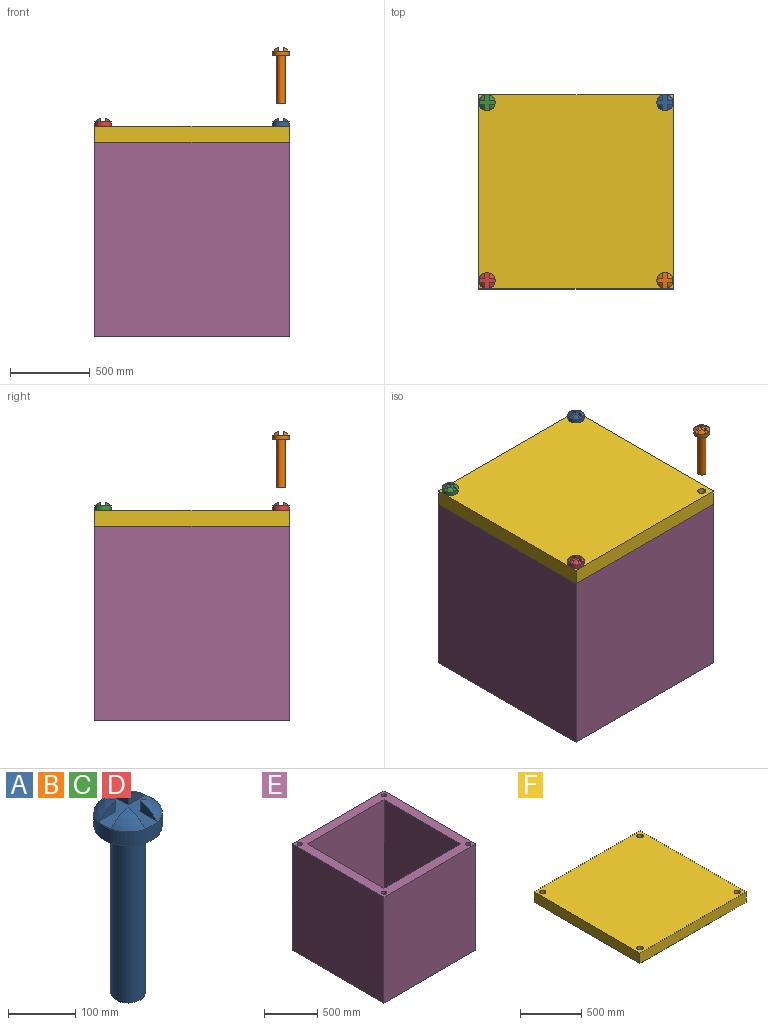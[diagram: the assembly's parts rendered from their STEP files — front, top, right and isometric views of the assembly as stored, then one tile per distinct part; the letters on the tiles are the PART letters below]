
ASSEMBLY  parts=6 mates=5
PART A: 14 faces, bbox 101.6x101.6x352.2 mm
  f0: revolved ~101.6x101.6mm, area 4783.2mm2, adj f4,f5,f6,f7,f8,f9,f10,f11
  f1: plane 50.8x50.8mm, normal (0,0,-1), area 2026.8mm2, adj f2
  f2: cylinder r=25.4mm len=304.8mm, axis (0,0,1), area 48643.9mm2, adj f1,f3
  f3: plane 101.6x101.6mm, normal (0,0,-1), area 6080.5mm2, adj f2,f4
  f4: cylinder r=50.8mm len=101.6mm, axis (0,0,1), area 8107.3mm2, adj f0,f3
  f5: plane 35.99x21.41mm, normal (0,1,0), area 474.5mm2, adj f0,f6,f13
  f6: plane 35.99x21.41mm, normal (1,0,0), area 474.5mm2, adj f0,f5,f13
  f7: plane 35.99x21.41mm, normal (-1,0,0), area 474.5mm2, adj f0,f8,f13
  f8: plane 35.99x21.41mm, normal (0,1,0), area 474.5mm2, adj f0,f7,f13
  f9: plane 35.99x21.41mm, normal (0,-1,0), area 474.5mm2, adj f0,f10,f13
  f10: plane 35.99x21.41mm, normal (-1,0,0), area 474.5mm2, adj f0,f9,f13
  f11: plane 35.99x21.41mm, normal (1,0,0), area 474.5mm2, adj f0,f12,f13
  f12: plane 35.99x21.41mm, normal (0,-1,0), area 474.5mm2, adj f0,f11,f13
  f13: plane 100.6x100.6mm, normal (0,0,1), area 4410.5mm2, adj f0,f5,f6,f7,f8,f9,f10,f11
PART B: same geometry as A
PART C: same geometry as A
PART D: same geometry as A
PART E: 19 faces, bbox 1219.2x1219.2x1219.2 mm
  f0: plane 1219.2x1219.2mm, normal (0,0,1), area 446085.3mm2, adj f1,f2,f3,f4,f6,f7,f8,f9
  f1: plane 1219.2x1219.2mm, normal (1,0,0), area 1486448.6mm2, adj f0,f2,f4,f5
  f2: plane 1219.2x1219.2mm, normal (0,1,0), area 1486448.6mm2, adj f0,f1,f3,f5
  f3: plane 1219.2x1219.2mm, normal (-1,0,0), area 1486448.6mm2, adj f0,f2,f4,f5
  f4: plane 1219.2x1219.2mm, normal (0,-1,0), area 1486448.6mm2, adj f0,f1,f3,f5
  f5: plane 1219.2x1219.2mm, normal (0,0,-1), area 1486448.6mm2, adj f1,f2,f3,f4
  f6: plane 1117.6x1016mm, normal (-1,0,0), area 1135481.6mm2, adj f0,f7,f9,f10
  f7: plane 1117.6x1016mm, normal (0,-1,0), area 1135481.6mm2, adj f0,f6,f8,f10
  f8: plane 1117.6x1016mm, normal (1,0,0), area 1135481.6mm2, adj f0,f7,f9,f10
  f9: plane 1117.6x1016mm, normal (0,1,0), area 1135481.6mm2, adj f0,f6,f8,f10
  f10: plane 1016x1016mm, normal (0,0,1), area 1032256mm2, adj f6,f7,f8,f9
  f11: cylinder r=25.4mm len=254mm, axis (0,0,1), area 40536.6mm2, adj f0,f12
  f12: plane 50.8x50.8mm, normal (0,0,1), area 2026.8mm2, adj f11
  f13: cylinder r=25.4mm len=254mm, axis (0,0,1), area 40536.6mm2, adj f0,f14
  f14: plane 50.8x50.8mm, normal (0,0,1), area 2026.8mm2, adj f13
  f15: cylinder r=25.4mm len=254mm, axis (0,0,1), area 40536.6mm2, adj f0,f16
  f16: plane 50.8x50.8mm, normal (0,0,1), area 2026.8mm2, adj f15
  f17: cylinder r=25.4mm len=254mm, axis (0,0,1), area 40536.6mm2, adj f0,f18
  f18: plane 50.8x50.8mm, normal (0,0,1), area 2026.8mm2, adj f17
PART F: 25 faces, bbox 1219.2x1219.2x203.2 mm
  f0: plane 1219.2x1219.2mm, normal (0,0,1), area 1478341.3mm2, adj f9,f10,f11,f12,f21,f22,f23,f24
  f1: plane 1219.2x1219.2mm, normal (0,0,-1), area 446085.3mm2, adj f4,f6,f9,f10,f11,f12,f13,f14
  f2: plane 1016x25.4mm, normal (-1,0,0), area 25806.4mm2, adj f8,f15,f16,f17
  f3: plane 965.2x50.8mm, normal (0,1,0), area 49032.2mm2, adj f17,f18,f19,f20
  f4: plane 1016x25.4mm, normal (1,0,0), area 25806.4mm2, adj f1,f6,f13,f18
  f5: plane 965.2x50.8mm, normal (0,-1,0), area 49032.2mm2, adj f17,f18,f19,f20
  f6: plane 1016x25.4mm, normal (0,1,0), area 25806.4mm2, adj f1,f4,f14,f18
  f7: plane 1016x25.4mm, normal (1,0,0), area 25806.4mm2, adj f8,f15,f16,f17
  f8: plane 1016x25.4mm, normal (0,-1,0), area 25806.4mm2, adj f2,f7,f16,f17
  f9: plane 1219.2x101.6mm, normal (1,0,0), area 123870.7mm2, adj f0,f1,f10,f12
  f10: plane 1219.2x101.6mm, normal (0,1,0), area 123870.7mm2, adj f0,f1,f9,f11
  f11: plane 1219.2x101.6mm, normal (-1,0,0), area 123870.7mm2, adj f0,f1,f10,f12
  f12: plane 1219.2x101.6mm, normal (0,-1,0), area 123870.7mm2, adj f0,f1,f9,f11
  f13: plane 1016x25.4mm, normal (0,-1,0), area 25806.4mm2, adj f1,f4,f14,f18
  f14: plane 1016x25.4mm, normal (-1,0,0), area 25806.4mm2, adj f1,f6,f13,f18
  f15: plane 1016x25.4mm, normal (0,1,0), area 25806.4mm2, adj f2,f7,f16,f17
  f16: plane 1016x1016mm, normal (0,0,-1), area 1032256mm2, adj f2,f7,f8,f15
  f17: plane 1016x1016mm, normal (0,0,1), area 100645mm2, adj f2,f3,f5,f7,f8,f15,f19,f20
  f18: plane 1016x1016mm, normal (0,0,-1), area 100645mm2, adj f3,f4,f5,f6,f13,f14,f19,f20
  f19: plane 965.2x50.8mm, normal (1,0,0), area 49032.2mm2, adj f3,f5,f17,f18
  f20: plane 965.2x50.8mm, normal (-1,0,0), area 49032.2mm2, adj f3,f5,f17,f18
  f21: cylinder r=25.4mm len=101.6mm, axis (0,0,1), area 16214.6mm2, adj f0,f1
  f22: cylinder r=25.4mm len=101.6mm, axis (0,0,1), area 16214.6mm2, adj f0,f1
  f23: cylinder r=25.4mm len=101.6mm, axis (0,0,1), area 16214.6mm2, adj f0,f1
  f24: cylinder r=25.4mm len=101.6mm, axis (0,0,1), area 16214.6mm2, adj f0,f1
PLACE A t=(408.61,788.55,602.89)mm
PLACE B t=(408.61,-329.05,1048)mm
PLACE C t=(-708.99,788.55,602.89)mm
PLACE D t=(-708.99,-329.05,602.89)mm
PLACE E t=(-150.19,229.75,-731.19)mm
PLACE F t=(-150.19,229.75,488.01)mm
MATE cylindrical C.f2 <-> F.f21  axis (0,0,1) through (-708.99,788.55,589.61)mm
MATE cylindrical D.f2 <-> F.f23  axis (0,0,1) through (-708.99,-329.05,589.61)mm
MATE cylindrical B.f2 <-> F.f22  axis (0,0,1) through (408.61,-329.05,1034.72)mm
MATE fastened F.f1 <-> E.f0  axis (0,0,-1) through (-150.19,-379.85,488.01)mm
MATE cylindrical A.f2 <-> F.f24  axis (0,0,1) through (408.61,788.55,589.61)mm
